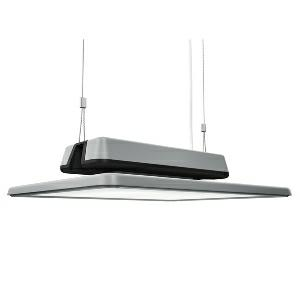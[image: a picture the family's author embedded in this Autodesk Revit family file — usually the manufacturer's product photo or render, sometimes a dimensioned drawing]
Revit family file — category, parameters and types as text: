
# Revit family: acaneo_-_hial_14000_840_w_ea_00737266_6e48
name_source: partatom
category: Lighting Fixtures
units: mm (PartAtom-declared; Revit-internal decimal feet)

## family parameters
Cut with Voids When Loaded = No
Host = Face
Light Source = No
Part Type = Normal
Room Calculation Point = No
Round Connector Dimension = Use Diameter
Shared = No

## types (1)
- ACANEO - HIAL 14000/840/W/EA (1 x LED, 15000 lm, 4000K)
    Apparent Load = 90 VA
    Approval mark = CE
    CIE Flux Codes = 76 97 99 100 100
    Color Rendering = 80-89
    Color Temperature = 4000K
    Control Gear = Electronic ballast
    Default Elevation = 1800 mm
    Description = HIAL 14000/840/W/EA|High bay luminaire|light source: LED|work equipment: Electronic ballast|connected load: 220-240 V, 50/60 Hz|Power consumption: approx. 90 W|power factor: approx. 0,950|luminous flux: 15000 lm|luminous efficacy: 166 lm/W|colour temperature: Cold white, ca. 4000 K|color rendering index (CRI): >= 80|chromaticity tolerance:  3 SDCM|System of protection: IP 65|class of protection: I|technology: Switchable|luminaire body|material: Aluminium|surface: Powder coatet|colour: White aluminium|lamp cover: Acrylic (PMMA), Clear|weight (net): approx. 8.2 kg|mains lead: Built-in plug RST 25i3 Einbau|Fastening: Available separately|Accessory: Junction box (RST 2013)|minimum ambient temperature: -30 ░C|maximum ambient temperature: 50 ░C|glare control: Optics|unified glare rating(4H 8H): <=  22|
    Frequency = 50 Hz, 60 Hz
    Height = 125 mm
    Lamp = 1 x LED
    Lamp Light Flux = 15000 lm
    Lamp count = 1
    Length = 480 mm
    Luminous efficacy = 167 lm/W
    Manufacturer = Waldmann
    ModVariant = No
    Model = 00737266
    Mounting Place = Ceiling
    Mounting Type = Pendant
    Number of Poles = 1
    OnlyDefault = Yes
    Power Factor = 1
    Product Name = ACANEO - HIAL 14000/840/W/EA
    Product group = High bay luminaire (industry)
    ProductGroupID = 901
    Protection Class = Protection class I
    Protection Degree = IP 65
    RLX_Detail_Level = 1
    RLX_Emergency_Light_Flux = 0 lm
    RLX_Emergency_Type = 0
    RLX_Emergency_Type_DB = No
    RlxData = <blob elided: 31161 chars, md5=655d0939>
    Socket = socket
    Standby Power = 0 W
    System Light Flux = 15000 lm
    System Power = 90 W
    Type Comments = Product without accessories
    Type Image = acaneo-hial.jpg
    URL = http://relux.com
    VarID = ---
    Voltage = 230 V
    Voltage Range = 110-120 V, 220-240 V
    Weight = 0.00 kg
    Width = 405 mm

## geometry (parser evidence)
native form markers: Blend x4, Sweep x11
no freeform markers — native parametric forms only
